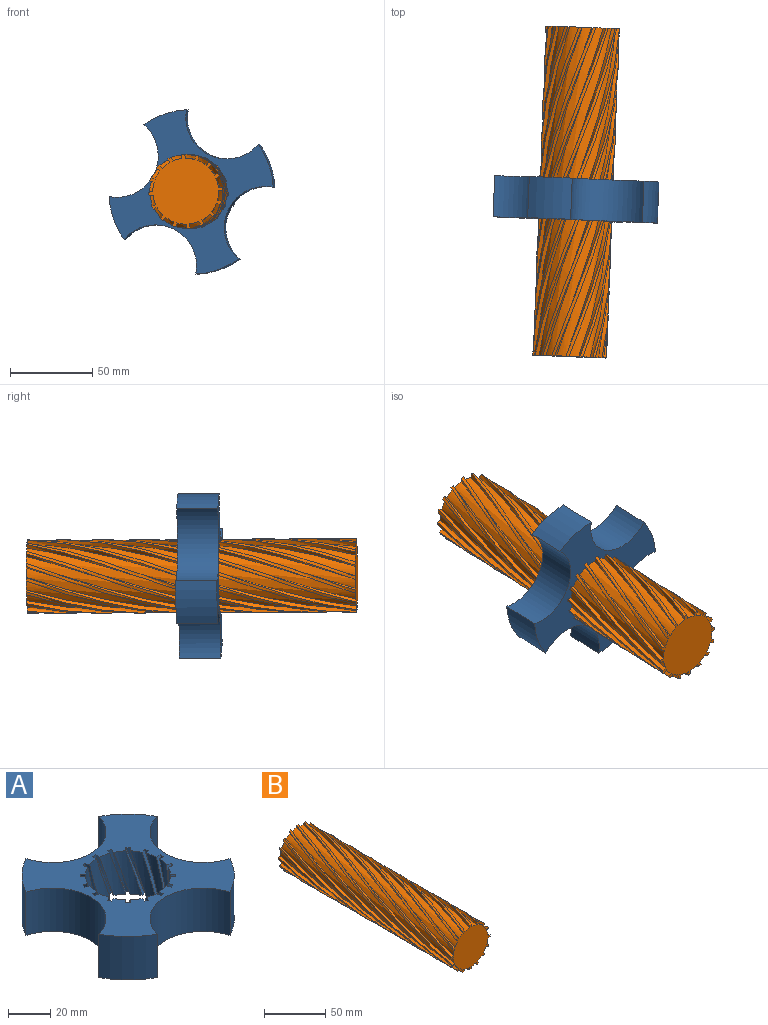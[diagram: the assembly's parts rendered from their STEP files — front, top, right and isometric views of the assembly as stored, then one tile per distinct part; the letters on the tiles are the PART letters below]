
ASSEMBLY  parts=2 mates=1
PART A: 74 faces, bbox 87.5x87.5x30.8 mm
  f0: cylinder r=20mm len=25mm, axis (0,0,-1), area 145.8mm2, adj f24,f25,f28,f72
  f1: cylinder r=20mm len=25mm, axis (0,0,-1), area 145.8mm2, adj f24,f25,f69,f73
  f2: cylinder r=20mm len=25mm, axis (0,0,-1), area 145.8mm2, adj f24,f25,f66,f70
  f3: cylinder r=20mm len=25mm, axis (0,0,-1), area 145.8mm2, adj f24,f25,f63,f67
  f4: cylinder r=20mm len=25mm, axis (0,0,-1), area 145.8mm2, adj f24,f25,f60,f64
  f5: cylinder r=20mm len=25mm, axis (0,0,-1), area 145.8mm2, adj f24,f25,f57,f61
  f6: cylinder r=20mm len=25mm, axis (0,0,-1), area 145.8mm2, adj f24,f25,f54,f58
  f7: cylinder r=20mm len=25mm, axis (0,0,-1), area 145.8mm2, adj f24,f25,f51,f55
  f8: cylinder r=20mm len=25mm, axis (0,0,-1), area 145.8mm2, adj f24,f25,f48,f52
  f9: cylinder r=20mm len=25mm, axis (0,0,-1), area 145.8mm2, adj f24,f25,f45,f49
  f10: cylinder r=20mm len=25mm, axis (0,0,-1), area 145.8mm2, adj f24,f25,f42,f46
  f11: cylinder r=20mm len=25mm, axis (0,0,-1), area 145.8mm2, adj f24,f25,f39,f43
  f12: cylinder r=20mm len=25mm, axis (0,0,-1), area 145.8mm2, adj f24,f25,f36,f40
  f13: cylinder r=20mm len=25mm, axis (0,0,-1), area 145.8mm2, adj f24,f25,f33,f37
  f14: cylinder r=20mm len=25mm, axis (0,0,-1), area 145.8mm2, adj f24,f25,f30,f34
  f15: cylinder r=20mm len=25mm, axis (0,0,-1), area 145.8mm2, adj f24,f25,f27,f31
  f16: cylinder r=25mm len=48.41mm, axis (0,0,-1), area 1647.6mm2, adj f17,f23,f24,f25
  f17: cylinder r=50mm len=25mm, axis (0,0,-1), area 700.1mm2, adj f16,f18,f24,f25
  f18: cylinder r=25mm len=48.41mm, axis (0,0,-1), area 1647.6mm2, adj f17,f19,f24,f25
  f19: cylinder r=50mm len=25mm, axis (0,0,-1), area 700.1mm2, adj f18,f20,f24,f25
  f20: cylinder r=25mm len=48.41mm, axis (0,0,-1), area 1647.6mm2, adj f19,f21,f24,f25
  f21: cylinder r=50mm len=25mm, axis (0,0,-1), area 700.1mm2, adj f20,f22,f24,f25
  f22: cylinder r=25mm len=48.41mm, axis (0,0,-1), area 1647.6mm2, adj f21,f23,f24,f25
  f23: cylinder r=50mm len=25mm, axis (0,0,-1), area 700.1mm2, adj f16,f22,f24,f25
  f24: plane 87.51x87.51mm, normal (0,0,1), area 3008.6mm2, adj f0,f1,f2,f3,f4,f5,f6,f7
  f25: plane 87.5x87.5mm, normal (0,0,-1), area 3008.8mm2, adj f0,f1,f2,f3,f4,f5,f6,f7
  f26: bspline ~30.77x12.36mm, area 50.5mm2, adj f24,f25,f27,f28
  f27: bspline ~30.77x10.34mm, area 66.4mm2, adj f15,f24,f25,f26
  f28: bspline ~30.77x10.57mm, area 66.4mm2, adj f0,f24,f25,f26
  f29: bspline ~25x8.94mm, area 50.5mm2, adj f24,f25,f30,f31
  f30: bspline ~30.77x9.54mm, area 66.4mm2, adj f14,f24,f25,f29
  f31: bspline ~30.77x10.11mm, area 66.4mm2, adj f15,f24,f25,f29
  f32: bspline ~30.77x10.89mm, area 50.5mm2, adj f24,f25,f33,f34
  f33: bspline ~30.77x10.36mm, area 66.4mm2, adj f13,f24,f25,f32
  f34: bspline ~30.77x9.86mm, area 66.4mm2, adj f14,f24,f25,f32
  f35: bspline ~25x10.55mm, area 50.5mm2, adj f24,f25,f36,f37
  f36: bspline ~30.77x10.72mm, area 66.4mm2, adj f12,f24,f25,f35
  f37: bspline ~30.77x10.57mm, area 66.4mm2, adj f13,f24,f25,f35
  f38: bspline ~30.77x12.36mm, area 50.5mm2, adj f24,f25,f39,f40
  f39: bspline ~30.77x10.34mm, area 66.4mm2, adj f11,f24,f25,f38
  f40: bspline ~30.77x10.57mm, area 66.4mm2, adj f12,f24,f25,f38
  f41: bspline ~25x8.94mm, area 50.5mm2, adj f24,f25,f42,f43
  f42: bspline ~30.77x9.54mm, area 66.4mm2, adj f10,f24,f25,f41
  f43: bspline ~30.77x10.11mm, area 66.4mm2, adj f11,f24,f25,f41
  f44: bspline ~30.77x10.89mm, area 50.5mm2, adj f24,f25,f45,f46
  f45: bspline ~30.77x10.36mm, area 66.4mm2, adj f9,f24,f25,f44
  f46: bspline ~30.77x9.86mm, area 66.4mm2, adj f10,f24,f25,f44
  f47: bspline ~25x10.55mm, area 50.5mm2, adj f24,f25,f48,f49
  f48: bspline ~30.77x10.72mm, area 66.4mm2, adj f8,f24,f25,f47
  f49: bspline ~30.77x10.57mm, area 66.4mm2, adj f9,f24,f25,f47
  f50: bspline ~30.77x12.36mm, area 50.5mm2, adj f24,f25,f51,f52
  f51: bspline ~30.77x10.34mm, area 66.4mm2, adj f7,f24,f25,f50
  f52: bspline ~30.77x10.57mm, area 66.4mm2, adj f8,f24,f25,f50
  f53: bspline ~25x8.94mm, area 50.5mm2, adj f24,f25,f54,f55
  f54: bspline ~30.77x9.54mm, area 66.4mm2, adj f6,f24,f25,f53
  f55: bspline ~30.77x10.11mm, area 66.4mm2, adj f7,f24,f25,f53
  f56: bspline ~30.77x10.89mm, area 50.5mm2, adj f24,f25,f57,f58
  f57: bspline ~30.77x10.36mm, area 66.4mm2, adj f5,f24,f25,f56
  f58: bspline ~30.77x9.86mm, area 66.4mm2, adj f6,f24,f25,f56
  f59: bspline ~25x10.55mm, area 50.5mm2, adj f24,f25,f60,f61
  f60: bspline ~30.77x10.72mm, area 66.4mm2, adj f4,f24,f25,f59
  f61: bspline ~30.77x10.57mm, area 66.4mm2, adj f5,f24,f25,f59
  f62: bspline ~30.77x12.36mm, area 50.5mm2, adj f24,f25,f63,f64
  f63: bspline ~30.77x10.34mm, area 66.4mm2, adj f3,f24,f25,f62
  f64: bspline ~30.77x10.57mm, area 66.4mm2, adj f4,f24,f25,f62
  f65: bspline ~25x8.94mm, area 50.5mm2, adj f24,f25,f66,f67
  f66: bspline ~30.77x9.54mm, area 66.4mm2, adj f2,f24,f25,f65
  f67: bspline ~30.77x10.11mm, area 66.4mm2, adj f3,f24,f25,f65
  f68: bspline ~30.77x10.89mm, area 50.5mm2, adj f24,f25,f69,f70
  f69: bspline ~30.77x10.36mm, area 66.4mm2, adj f1,f24,f25,f68
  f70: bspline ~30.77x9.86mm, area 66.4mm2, adj f2,f24,f25,f68
  f71: bspline ~25x10.55mm, area 50.5mm2, adj f24,f25,f72,f73
  f72: bspline ~30.77x10.72mm, area 66.4mm2, adj f0,f24,f25,f71
  f73: bspline ~30.77x10.57mm, area 66.4mm2, adj f1,f24,f25,f71
PART B: 66 faces, bbox 45.3x215.4x45.3 mm
  f0: cylinder r=20mm len=200mm, axis (0,1,0), area 1170.6mm2, adj f16,f17,f19,f63
  f1: cylinder r=20mm len=200mm, axis (0,1,0), area 1170.6mm2, adj f16,f17,f59,f61
  f2: cylinder r=20mm len=200mm, axis (0,1,0), area 1170.6mm2, adj f16,f17,f56,f58
  f3: cylinder r=20mm len=200mm, axis (0,1,0), area 1170.6mm2, adj f16,f17,f53,f55
  f4: cylinder r=20mm len=200mm, axis (0,1,0), area 1170.6mm2, adj f16,f17,f50,f52
  f5: cylinder r=20mm len=200mm, axis (0,1,0), area 1170.6mm2, adj f16,f17,f47,f49
  f6: cylinder r=20mm len=200mm, axis (0,1,0), area 1170.6mm2, adj f16,f17,f44,f46
  f7: cylinder r=20mm len=200mm, axis (0,1,0), area 1170.6mm2, adj f16,f17,f41,f43
  f8: cylinder r=20mm len=200mm, axis (0,1,0), area 1170.6mm2, adj f16,f17,f38,f40
  f9: cylinder r=20mm len=200mm, axis (0,1,0), area 1170.6mm2, adj f16,f17,f35,f37
  f10: cylinder r=20mm len=200mm, axis (0,1,0), area 1170.6mm2, adj f16,f17,f32,f34
  f11: cylinder r=20mm len=200mm, axis (0,1,0), area 1170.6mm2, adj f16,f17,f29,f31
  f12: cylinder r=20mm len=200mm, axis (0,1,0), area 1170.6mm2, adj f16,f17,f26,f28
  f13: cylinder r=20mm len=200mm, axis (0,1,0), area 1170.6mm2, adj f16,f17,f23,f25
  f14: cylinder r=20mm len=200mm, axis (0,1,0), area 1170.6mm2, adj f16,f17,f20,f22
  f15: cylinder r=20mm len=200mm, axis (0,1,0), area 1170.6mm2, adj f16,f17,f62,f64
  f16: plane 44.95x44.95mm, normal (0,-1,0), area 1336.1mm2, adj f0,f1,f2,f3,f4,f5,f6,f7
  f17: plane 44.95x44.95mm, normal (0,1,0), area 1336.1mm2, adj f0,f1,f2,f3,f4,f5,f6,f7
  f18: bspline ~215.38x45.03mm, area 400mm2, adj f16,f17,f19,f20
  f19: bspline ~215.38x45.03mm, area 527mm2, adj f0,f16,f17,f18
  f20: bspline ~215.38x44.67mm, area 527mm2, adj f14,f16,f17,f18
  f21: bspline ~215.38x42.41mm, area 400mm2, adj f16,f17,f22,f23
  f22: bspline ~215.38x42.29mm, area 527mm2, adj f14,f16,f17,f21
  f23: bspline ~215.38x41.37mm, area 527mm2, adj f13,f16,f17,f21
  f24: bspline ~215.38x43.81mm, area 400mm2, adj f16,f17,f25,f26
  f25: bspline ~215.38x42.98mm, area 527mm2, adj f13,f16,f17,f24
  f26: bspline ~215.38x43.81mm, area 527mm2, adj f12,f16,f17,f24
  f27: bspline ~215.38x45.19mm, area 400mm2, adj f16,f17,f28,f29
  f28: bspline ~215.38x45.07mm, area 527mm2, adj f12,f16,f17,f27
  f29: bspline ~215.38x45.19mm, area 527mm2, adj f11,f16,f17,f27
  f30: bspline ~215.38x45.03mm, area 400mm2, adj f16,f17,f31,f32
  f31: bspline ~215.38x45.03mm, area 527mm2, adj f11,f16,f17,f30
  f32: bspline ~215.38x44.67mm, area 527mm2, adj f10,f16,f17,f30
  f33: bspline ~215.38x42.41mm, area 400mm2, adj f16,f17,f34,f35
  f34: bspline ~215.38x42.29mm, area 527mm2, adj f10,f16,f17,f33
  f35: bspline ~215.38x41.37mm, area 527mm2, adj f9,f16,f17,f33
  f36: bspline ~215.38x43.81mm, area 400mm2, adj f16,f17,f37,f38
  f37: bspline ~215.38x42.98mm, area 527mm2, adj f9,f16,f17,f36
  f38: bspline ~215.38x43.81mm, area 527mm2, adj f8,f16,f17,f36
  f39: bspline ~215.38x45.19mm, area 400mm2, adj f16,f17,f40,f41
  f40: bspline ~215.38x45.07mm, area 527mm2, adj f8,f16,f17,f39
  f41: bspline ~215.38x45.19mm, area 527mm2, adj f7,f16,f17,f39
  f42: bspline ~215.38x45.03mm, area 400mm2, adj f16,f17,f43,f44
  f43: bspline ~215.38x45.03mm, area 527mm2, adj f7,f16,f17,f42
  f44: bspline ~215.38x44.67mm, area 527mm2, adj f6,f16,f17,f42
  f45: bspline ~215.38x42.41mm, area 400mm2, adj f16,f17,f46,f47
  f46: bspline ~215.38x42.29mm, area 527mm2, adj f6,f16,f17,f45
  f47: bspline ~215.38x41.37mm, area 527mm2, adj f5,f16,f17,f45
  f48: bspline ~215.38x43.81mm, area 400mm2, adj f16,f17,f49,f50
  f49: bspline ~215.38x42.98mm, area 527mm2, adj f5,f16,f17,f48
  f50: bspline ~215.38x43.81mm, area 527mm2, adj f4,f16,f17,f48
  f51: bspline ~215.38x45.19mm, area 400mm2, adj f16,f17,f52,f53
  f52: bspline ~215.38x45.07mm, area 527mm2, adj f4,f16,f17,f51
  f53: bspline ~215.38x45.19mm, area 527mm2, adj f3,f16,f17,f51
  f54: bspline ~215.38x45.03mm, area 400mm2, adj f16,f17,f55,f56
  f55: bspline ~215.38x45.03mm, area 527mm2, adj f3,f16,f17,f54
  f56: bspline ~215.38x44.67mm, area 527mm2, adj f2,f16,f17,f54
  f57: bspline ~215.38x42.41mm, area 400mm2, adj f16,f17,f58,f59
  f58: bspline ~215.38x42.29mm, area 527mm2, adj f2,f16,f17,f57
  f59: bspline ~215.38x41.37mm, area 527mm2, adj f1,f16,f17,f57
  f60: bspline ~215.38x43.81mm, area 400mm2, adj f16,f17,f61,f62
  f61: bspline ~215.38x42.98mm, area 527mm2, adj f1,f16,f17,f60
  f62: bspline ~215.38x43.81mm, area 527mm2, adj f15,f16,f17,f60
  f63: bspline ~215.38x45.19mm, area 527mm2, adj f0,f16,f17,f65
  f64: bspline ~215.38x45.07mm, area 527mm2, adj f15,f16,f17,f65
  f65: bspline ~215.38x45.19mm, area 400mm2, adj f16,f17,f63,f64
PLACE A rot(axis=(-0.75,-0.45,-0.48),107.7deg) t=(-29.88,-87.46,140.46)mm
PLACE B rot(axis=(-0.02,-1,0),139deg) t=(-25.25,29.45,139.88)mm
MATE cylindrical A.f17 <-> B.f0  axis (-0.04,-1,0) through (-29.88,-87.46,140.46)mm
